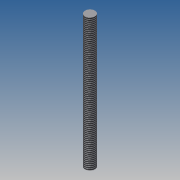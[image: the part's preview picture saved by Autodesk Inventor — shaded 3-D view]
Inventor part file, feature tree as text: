
AUTODESK INVENTOR PART (.ipt)
format: ipt  version: 2015 SP1 (Build 190203100, 203)  size: 73,216 bytes
history: native  units: mm
features: extrude x1, thread x1, sketch x1
ambient origin geometry x8: Origin, YZ Plane, XZ Plane, XY Plane, X Axis, Y Axis, Z Axis, Center Point
bodies: Volumenkörper1 (feature_tree)
feature tree (3):
  extrude  "Extrusion1"  Depth=40.0mm TaperAngle=0.0deg
  thread  "Gewinde1"  [1 undecoded]
  sketch  "Skizze1"  dims[d0=3.0mm d1=40.0mm d2=0.0mm d3=10.0mm d4=0.0mm]
note: 1 required parameter value undecoded (feature->parameter linkage not recoverable at this tier; creation-order binding heuristic only, values carry confidence <= 0.55)
